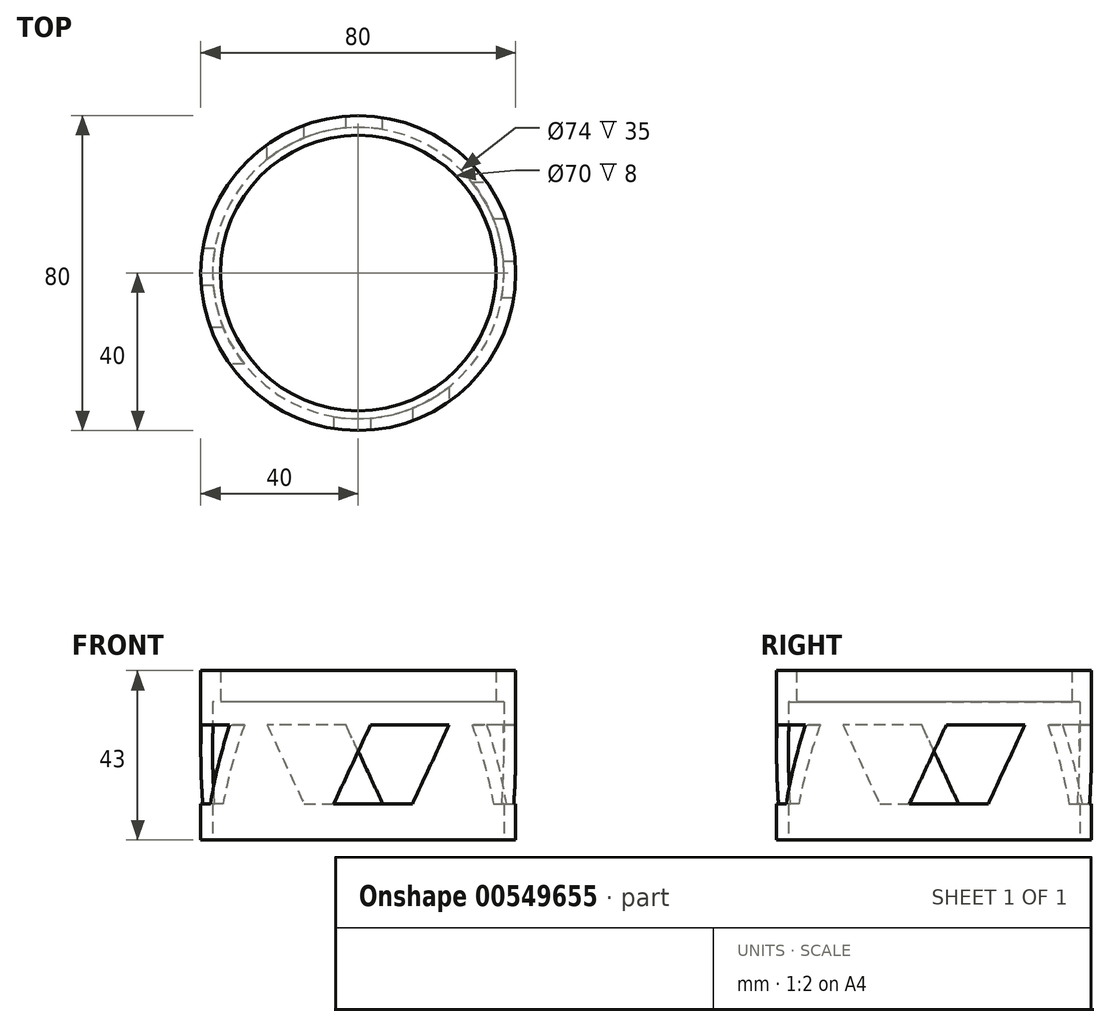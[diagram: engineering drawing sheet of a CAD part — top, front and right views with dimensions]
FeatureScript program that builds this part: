
annotation { "Feature Type Name" : "Feature", "Feature Type Description" : "" }
export const myFeature = defineFeature(function(context is Context, id is Id, definition is map)
    precondition{}
    {
        {
            var Q0;
            Q0=qCreatedBy(makeId("Top.planeOp"),FACE);
            var sketch = newSketch(context, id + "F0", { "sketchPlane" : qUnion([Q0])});
            skCircle(sketch, "E0", {"center": v(0, 0) * mm, "radius": 37 * mm});
            skCircle(sketch, "E1", {"center": v(0, 0) * mm, "radius": 40 * mm});
            skSolve(sketch);
        }
        {
            var Q0;
            Q0 = qSketchRegion(id + "F0", true);
            extrude(context, id + "F1", {"entities" : qUnion([Q0]), "depth" : 5 * mm, "offsetDistance" : 25 * mm});
        }
        {
            var Q0;
            Q0 = qSketchRegion(id + "F0", true);
            extrude(context, id + "F2", {"entities" : qUnion([Q0]), "operationType" : NewBodyOperationType.ADD, "oppositeDirection" : true, "depth" : 35 * mm, "offsetDistance" : 25 * mm});
        }
        {
            var Q0;
            Q0=qCreatedBy(makeId("Top.planeOp"),FACE);
            var sketch = newSketch(context, id + "F3", { "sketchPlane" : qUnion([Q0])});
            skCircle(sketch, "E2", {"center": v(0, 0) * mm, "radius": 35 * mm});
            skCircle(sketch, "E3", {"center": v(0, 0) * mm, "radius": 40 * mm});
            skSolve(sketch);
        }
        {
            var Q0;
            Q0 = qSketchRegion(id + "F3", true);
            extrude(context, id + "F4", {"entities" : qUnion([Q0]), "operationType" : NewBodyOperationType.ADD, "depth" : 8 * mm, "offsetDistance" : 25 * mm});
        }
        {
            var Q0;
            Q0=qCreatedBy(makeId("Front.planeOp"),FACE);
            cPlane(context, id + "F5", {"entities" : qUnion([Q0]), "cplaneType" : CPlaneType.OFFSET, "offset" : 50 * mm, "width" : 150 * mm, "height" : 150 * mm});
        }
        {
            var Q0;
            Q0=qCreatedBy(id+"F5.planeOp",FACE);
            var sketch = newSketch(context, id + "F6", { "sketchPlane" : qUnion([Q0])});
            skLineSegment(sketch, "E4", {"start": v(-6.2, -25.8) * mm, "end": v(13.8, -25.8) * mm});
            skLineSegment(sketch, "E5", {"start": v(13.8, -25.8) * mm, "end": v(23.12, -5.8) * mm});
            skLineSegment(sketch, "E6", {"start": v(23.12, -5.8) * mm, "end": v(3.12, -5.8) * mm});
            skLineSegment(sketch, "E7", {"start": v(3.12, -5.8) * mm, "end": v(-6.2, -25.8) * mm});
            skSolve(sketch);
        }
        {
            var Q0;
            Q0 = qSketchRegion(id + "F6", true);
            extrude(context, id + "F7", {"entities" : qUnion([Q0]), "oppositeDirection" : true, "depth" : 35 * mm, "offsetDistance" : 25 * mm});
        }
        {
            var Q0;
            Q0=qCreatedBy(makeId("Front.planeOp"),FACE);
            var sketch = newSketch(context, id + "F8", { "sketchPlane" : qUnion([Q0])});
            skLineSegment(sketch, "E8", {"start": v(0, 0) * mm, "end": v(0, -40.8) * mm, "construction": true});
            skSolve(sketch);
        }
        {
            var Q0;
            Q0=makeQuery(id+"F7.opExtrude","SWEPT_BODY",BODY,{"disambiguationData":[OSD([sQuery(id+"F6.wireOp",EDGE,"E4"),sQuery(id+"F6.wireOp",EDGE,"E5"),sQuery(id+"F6.wireOp",EDGE,"E6"),sQuery(id+"F6.wireOp",EDGE,"E7")])]});
            var Q1;
            Q1=sQuery(id+"F8.wireOp",EDGE,"E8");
            circularPattern(context, id + "F9", {"operationType" : NewBodyOperationType.REMOVE, "entities" : qUnion([Q0]), "axis" : qUnion([Q1]), "angle" : 360 * degree, "instanceCount" : 4, "equalSpace" : true});
        }
    });
